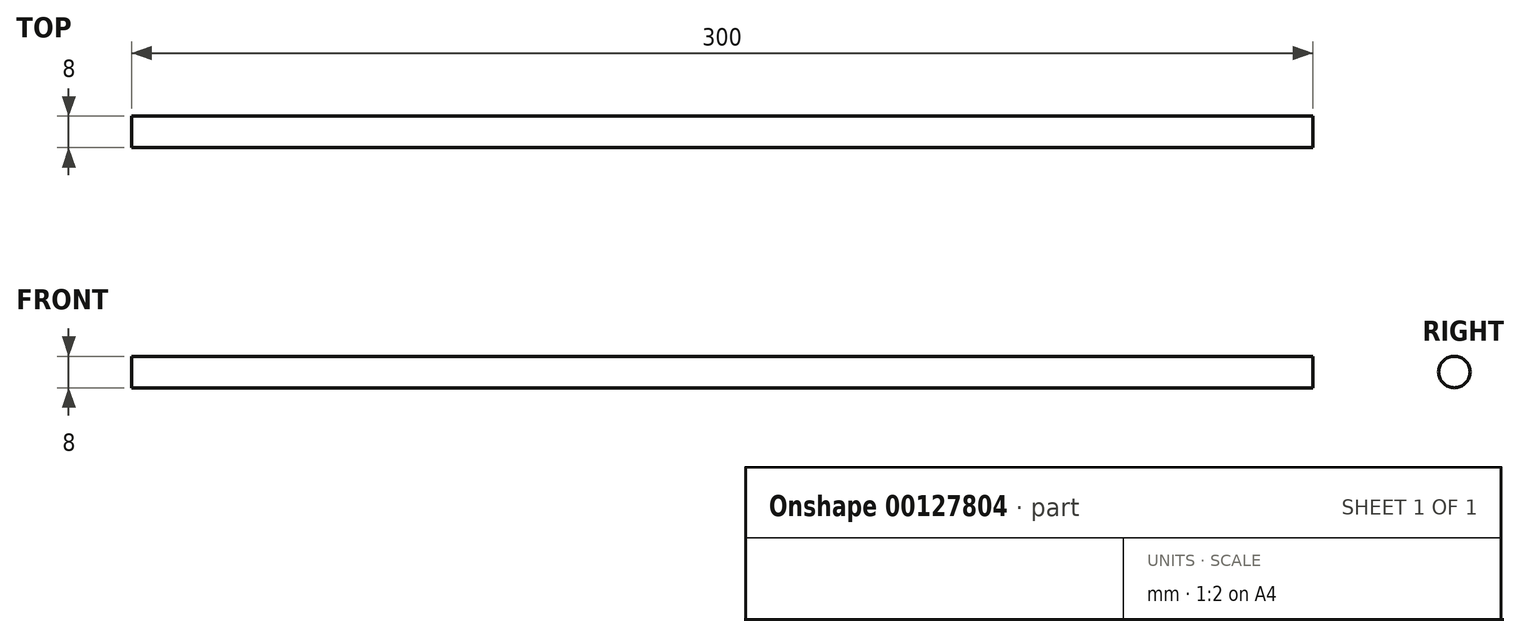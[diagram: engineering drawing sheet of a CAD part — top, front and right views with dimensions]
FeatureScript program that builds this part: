
annotation { "Feature Type Name" : "Feature", "Feature Type Description" : "" }
export const myFeature = defineFeature(function(context is Context, id is Id, definition is map)
    precondition{}
    {
        {
            var Q0;
            Q0=qCreatedBy(makeId("Top.planeOp"),FACE);
            var sketch = newSketch(context, id + "F0", { "sketchPlane" : qUnion([Q0])});
            skLineSegment(sketch, "E0", {"start": v(-150, 0) * mm, "end": v(150, 0) * mm});
            skLineSegment(sketch, "E1", {"start": v(150, 0) * mm, "end": v(150, 4) * mm});
            skLineSegment(sketch, "E2", {"start": v(150, 4) * mm, "end": v(-150, 4) * mm});
            skLineSegment(sketch, "E3", {"start": v(-150, 4) * mm, "end": v(-150, 0) * mm});
            skLineSegment(sketch, "E4", {"start": v(0, 0) * mm, "end": v(268.79, 0) * mm, "construction": true});
            skSolve(sketch);
        }
        {
            var Q0;
            Q0 = qSketchRegion(id + "F0", true);
            var Q1;
            Q1=sQuery(id+"F0.wireOp",EDGE,"E4");
            revolve(context, id + "F1", {"entities" : qUnion([Q0]), "axis" : qUnion([Q1]), "revolveType" : RevolveType.FULL});
        }
    });
